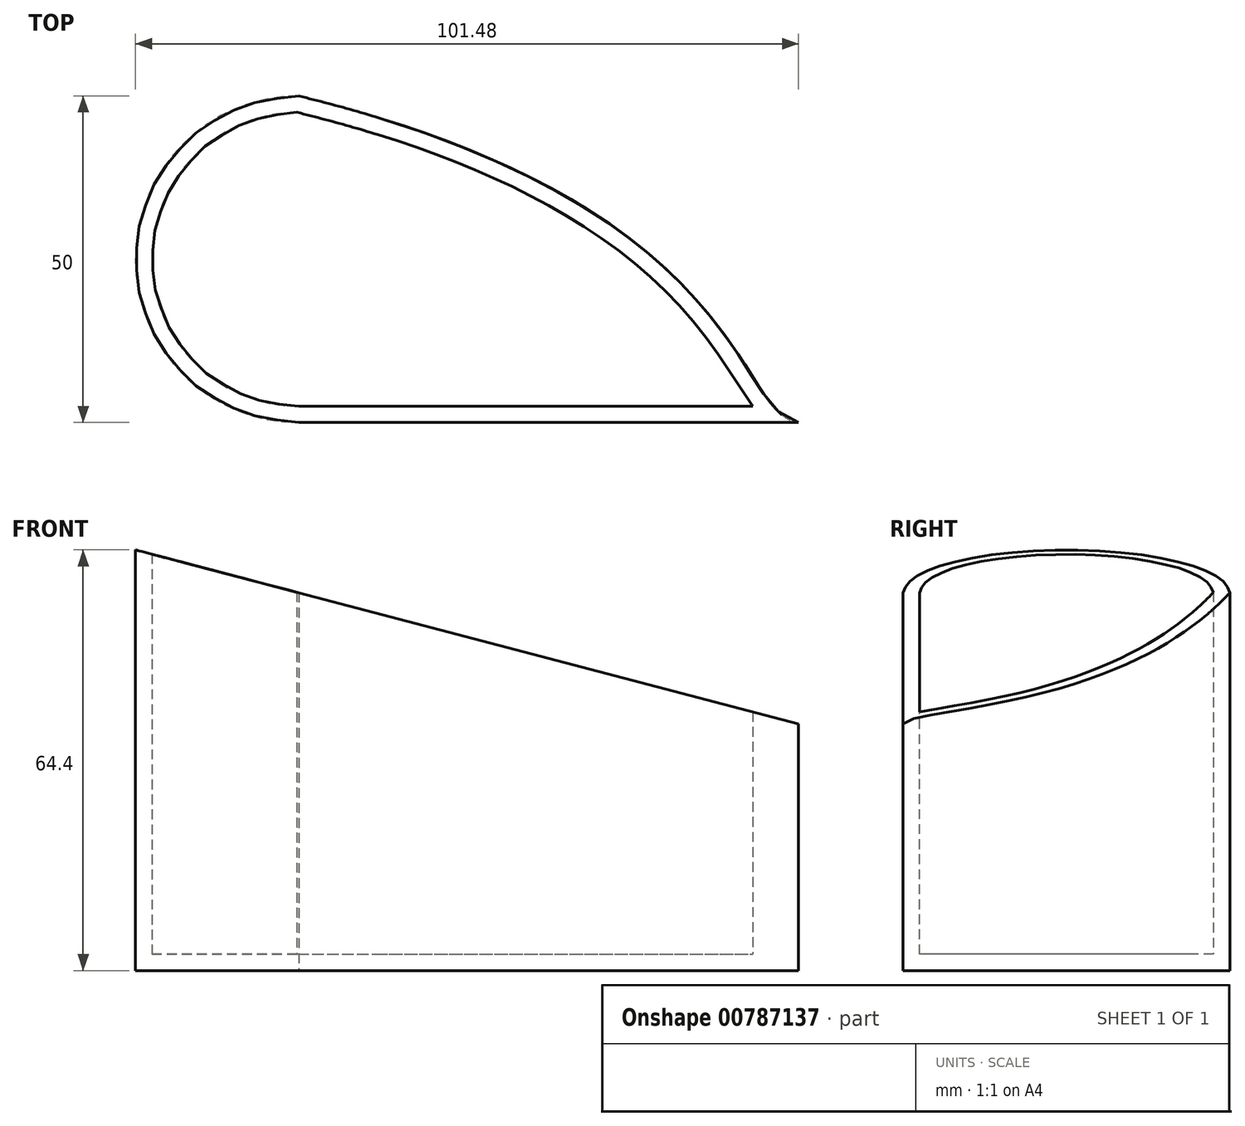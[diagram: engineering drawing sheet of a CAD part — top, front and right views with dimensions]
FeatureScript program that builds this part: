
annotation { "Feature Type Name" : "Feature", "Feature Type Description" : "" }
export const myFeature = defineFeature(function(context is Context, id is Id, definition is map)
    precondition{}
    {
        {
            var Q0;
            Q0=qCreatedBy(makeId("Top.planeOp"),FACE);
            var sketch = newSketch(context, id + "F0", { "sketchPlane" : qUnion([Q0])});
            skCircle(sketch, "E0", {"center": v(0, 0) * mm, "radius": 25 * mm});
            skLineSegment(sketch, "E1", {"start": v(0, -25) * mm, "end": v(76.48, -25) * mm});
            skFitSpline(sketch, "E2", {"points": [v(0, 25) * mm, v(76.48, -25) * mm, v(92.25, -15.14) * mm], "startDerivative": vector(301.09, -73.52) * mm, "endDerivative": vector(41.37, 47.9) * mm});
            skSolve(sketch);
        }
        {
            var Q0;
            {var subQ0=sQuery(id+"F0.wireOp",EDGE,"E0");var subQ1=makeQuery(id+"F0.imprint","INTERSECT",VERTEX,{"derivedFrom":[subQ0,sQuery(id+"F0.wireOp",EDGE,"E1")]});Q0=makeQuery(id+"F0.imprint","IMPRINT",FACE,{"disambiguationData":[TD([[makeQuery(id+"F0.imprint","IMPRINT",EDGE,{"disambiguationData":[TD([[subQ1,1.0]])],"derivedFrom":subQ0}),1.0]])]});}
            var Q1;
            {var subQ0=sQuery(id+"F0.wireOp",EDGE,"E1");Q1=makeQuery(id+"F0.imprint","IMPRINT",FACE,{"disambiguationData":[TD([[makeQuery(id+"F0.imprint","IMPRINT",EDGE,{"derivedFrom":subQ0}),1.0]])]});}
            extrude(context, id + "F1", {"entities" : qUnion([Q0, Q1]), "depth" : 64.4 * mm, "offsetDistance" : 25 * mm});
        }
        {
            var Q0;
            Q0=qCreatedBy(makeId("Front.planeOp"),FACE);
            var sketch = newSketch(context, id + "F2", { "sketchPlane" : qUnion([Q0])});
            skLineSegment(sketch, "E3.0.0", {"start": v(0, 0) * mm, "end": v(76.48, 0) * mm});
            skLineSegment(sketch, "E3.0.1", {"start": v(76.48, 0) * mm, "end": v(76.48, 64.4) * mm});
            skLineSegment(sketch, "E3.0.2", {"start": v(76.48, 64.4) * mm, "end": v(0, 64.4) * mm});
            skLineSegment(sketch, "E3.0.3", {"start": v(0, 64.4) * mm, "end": v(0, 0) * mm});
            skLineSegment(sketch, "E4", {"start": v(-25, 0) * mm, "end": v(-25, 64.4) * mm});
            skLineSegment(sketch, "E5.0", {"start": v(0, 64.4) * mm, "end": v(-25, 64.4) * mm});
            skLineSegment(sketch, "E6.0", {"start": v(0, 0) * mm, "end": v(-25, 0) * mm});
            skLineSegment(sketch, "E7", {"start": v(-25, 64.4) * mm, "end": v(76.48, 37.76) * mm});
            skSolve(sketch);
        }
        {
            var Q0;
            {var subQ0=sQuery(id+"F2.wireOp",EDGE,"E5.0");Q0=makeQuery(id+"F2.imprint","IMPRINT",FACE,{"disambiguationData":[TD([[makeQuery(id+"F2.imprint","IMPRINT",EDGE,{"derivedFrom":subQ0}),1.0]])]});}
            var Q1;
            {var subQ0=sQuery(id+"F2.wireOp",EDGE,"E3.0.2");Q1=makeQuery(id+"F2.imprint","IMPRINT",FACE,{"disambiguationData":[TD([[makeQuery(id+"F2.imprint","IMPRINT",EDGE,{"derivedFrom":subQ0}),1.0]])]});}
            extrude(context, id + "F3", {"entities" : qUnion([Q0, Q1]), "operationType" : NewBodyOperationType.REMOVE, "endBound" : BoundingType.THROUGH_ALL, "oppositeDirection" : true, "depth" : 25 * mm, "offsetDistance" : 25 * mm, "hasSecondDirection" : true, "secondDirectionBound" : SecondDirectionBoundingType.THROUGH_ALL, "secondDirectionOppositeDirection" : false, "secondDirectionDepth" : 25 * mm});
        }
        {
            var Q0;
            Q0=makeQuery(id+"F3.boolean.opBoolean","COPY",FACE,{"derivedFrom":makeQuery(id+"F3.opExtrude","SWEPT_FACE",FACE,{"disambiguationData":[OSD([sQuery(id+"F2.wireOp",EDGE,"E7")])]})});
            shell(context, id + "F4", {"entities" : qUnion([Q0]), "thickness" : 2.5 * mm});
        }
    });
